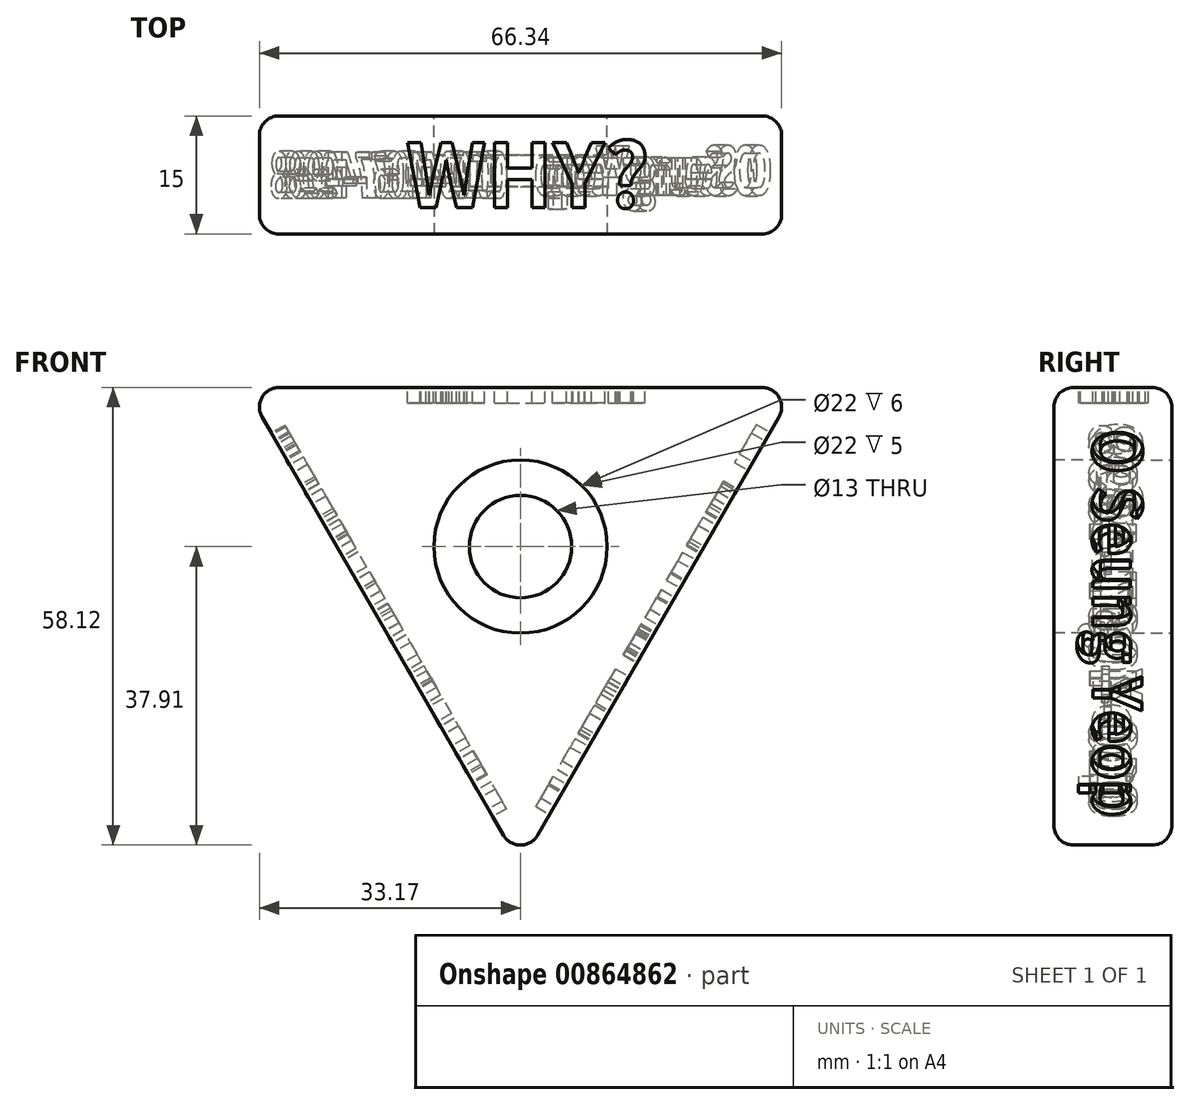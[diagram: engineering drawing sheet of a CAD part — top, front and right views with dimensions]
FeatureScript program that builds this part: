
annotation { "Feature Type Name" : "Feature", "Feature Type Description" : "" }
export const myFeature = defineFeature(function(context is Context, id is Id, definition is map)
    precondition{}
    {
        {
            var Q0;
            Q0=qCreatedBy(makeId("Front.planeOp"),FACE);
            var sketch = newSketch(context, id + "F0", { "sketchPlane" : qUnion([Q0])});
            skCircle(sketch, "E0.cCircle", {"center": v(0, 0) * mm, "radius": 20.2 * mm, "construction": true});
            skLineSegment(sketch, "E0.0", {"start": v(-35, 20.2) * mm, "end": v(35, 20.2) * mm});
            skLineSegment(sketch, "E0.1", {"start": v(35, 20.2) * mm, "end": v(0, -40.41) * mm});
            skLineSegment(sketch, "E0.2", {"start": v(0, -40.41) * mm, "end": v(-35, 20.2) * mm});
            skPoint(sketch, "E0.0.midPoint", {"position": v(0, 20.2) * mm});
            skSolve(sketch);
        }
        {
            var Q0;
            Q0 = qSketchRegion(id + "F0", true);
            extrude(context, id + "F1", {"entities" : qUnion([Q0]), "depth" : 15 * mm, "offsetDistance" : 25 * mm});
        }
        {
            var Q0;
            Q0=makeQuery(id+"F1.opExtrude","SWEPT_FACE",FACE,{"disambiguationData":[OSD([sQuery(id+"F0.wireOp",EDGE,"E0.0")])]});
            var sketch = newSketch(context, id + "F2", { "sketchPlane" : qUnion([Q0])});
            skText(sketch, "E1", { "text": "WHY?", "fontName": "NotoSansCJKkr-Bold.otf"});
            const initialGuessF2  = {"E1": [-0.01455, -0.01164, 1, 0, 0.00805]};
            skSetInitialGuess(sketch, initialGuessF2);
            skSolve(sketch);
        }
        {
            var Q0;
            Q0 = qSketchRegion(id + "F2", true);
            extrude(context, id + "F3", {"entities" : qUnion([Q0]), "operationType" : NewBodyOperationType.REMOVE, "oppositeDirection" : true, "depth" : 2 * mm, "offsetDistance" : 25 * mm});
        }
        {
            var Q0;
            Q0=makeQuery(id+"F1.opExtrude","CAP_FACE",FACE,{"disambiguationData":[OSD([sQuery(id+"F0.wireOp",EDGE,"E0.0"),sQuery(id+"F0.wireOp",EDGE,"E0.1"),sQuery(id+"F0.wireOp",EDGE,"E0.2")])],"isStart":false});
            var sketch = newSketch(context, id + "F4", { "sketchPlane" : qUnion([Q0])});
            skCircle(sketch, "E2", {"center": v(0, 0) * mm, "radius": 11 * mm});
            skSolve(sketch);
        }
        {
            var Q0;
            Q0=makeQuery(id+"F4.imprint","IMPRINT",FACE,{"disambiguationData":[TD([[makeQuery(id+"F4.imprint","IMPRINT",EDGE,{"derivedFrom":sQuery(id+"F4.wireOp",EDGE,"E2")}),1.0]])]});
            var Q1;
            Q1 = qSketchRegion(id + "F6", true);
            extrude(context, id + "F5", {"entities" : qUnion([Q0, Q1]), "operationType" : NewBodyOperationType.REMOVE, "oppositeDirection" : true, "depth" : 6 * mm, "offsetDistance" : 25 * mm});
        }
        {
            var Q0;
            Q0=makeQuery(id+"F1.opExtrude","CAP_FACE",FACE,{"disambiguationData":[OSD([sQuery(id+"F0.wireOp",EDGE,"E0.0"),sQuery(id+"F0.wireOp",EDGE,"E0.1"),sQuery(id+"F0.wireOp",EDGE,"E0.2")])],"isStart":true});
            var sketch = newSketch(context, id + "F6", { "sketchPlane" : qUnion([Q0])});
            skCircle(sketch, "E3", {"center": v(0, 0) * mm, "radius": 11 * mm});
            skSolve(sketch);
        }
        {
            var Q0;
            Q0=makeQuery(id+"F6.imprint","IMPRINT",FACE,{"disambiguationData":[TD([[makeQuery(id+"F6.imprint","IMPRINT",EDGE,{"derivedFrom":sQuery(id+"F6.wireOp",EDGE,"E3")}),1.0]])]});
            extrude(context, id + "F7", {"entities" : qUnion([Q0]), "operationType" : NewBodyOperationType.REMOVE, "oppositeDirection" : true, "depth" : 5 * mm, "offsetDistance" : 25 * mm});
        }
        {
            var Q0;
            Q0=makeQuery(id+"F5.boolean.opBoolean","COPY",FACE,{"derivedFrom":makeQuery(id+"F5.opExtrude","CAP_FACE",FACE,{"disambiguationData":[OSD([sQuery(id+"F4.wireOp",EDGE,"E2")])],"isStart":false})});
            var sketch = newSketch(context, id + "F8", { "sketchPlane" : qUnion([Q0])});
            skCircle(sketch, "E4", {"center": v(0, 0) * mm, "radius": 6.5 * mm});
            skSolve(sketch);
        }
        {
            var Q0;
            Q0=makeQuery(id+"F8.imprint","IMPRINT",FACE,{"disambiguationData":[TD([[makeQuery(id+"F8.imprint","IMPRINT",EDGE,{"derivedFrom":sQuery(id+"F8.wireOp",EDGE,"E4")}),1.0]])]});
            extrude(context, id + "F9", {"entities" : qUnion([Q0]), "operationType" : NewBodyOperationType.REMOVE, "oppositeDirection" : true, "depth" : 25 * mm, "offsetDistance" : 25 * mm});
        }
        {
            var Q0;
            Q0=makeQuery(id+"F1.opExtrude","SWEPT_FACE",FACE,{"disambiguationData":[OSD([sQuery(id+"F0.wireOp",EDGE,"E0.1")])]});
            var sketch = newSketch(context, id + "F10", { "sketchPlane" : qUnion([Q0])});
            skText(sketch, "E5", { "text": "O Seung Yeop", "fontName": "NotoSansCJKkr-Bold.otf"});
            const initialGuessF10  = {"E5": [-0.01004, 0.02888, 0, -1, 0.00608]};
            skSetInitialGuess(sketch, initialGuessF10);
            skSolve(sketch);
        }
        {
            var Q0;
            Q0 = qSketchRegion(id + "F10", true);
            extrude(context, id + "F11", {"entities" : qUnion([Q0]), "operationType" : NewBodyOperationType.REMOVE, "oppositeDirection" : true, "depth" : 2 * mm, "offsetDistance" : 25 * mm});
        }
        {
            var Q0;
            Q0=makeQuery(id+"F1.opExtrude","SWEPT_FACE",FACE,{"disambiguationData":[OSD([sQuery(id+"F0.wireOp",EDGE,"E0.2")])]});
            var sketch = newSketch(context, id + "F12", { "sketchPlane" : qUnion([Q0])});
            skText(sketch, "E6", { "text": "010-4067-4998", "fontName": "NotoSansCJKkr-Bold.otf"});
            const initialGuessF12  = {"E6": [0.01042, -0.02829, 0, 1, 0.00568]};
            skSetInitialGuess(sketch, initialGuessF12);
            skSolve(sketch);
        }
        {
            var Q0;
            Q0 = qSketchRegion(id + "F12", true);
            extrude(context, id + "F13", {"entities" : qUnion([Q0]), "operationType" : NewBodyOperationType.REMOVE, "oppositeDirection" : true, "depth" : 2 * mm, "offsetDistance" : 25 * mm});
        }
        {
            var Q0;
            Q0=makeQuery(id+"F1.opExtrude","CAP_EDGE",EDGE,{"disambiguationData":[OSD([sQuery(id+"F0.wireOp",EDGE,"E0.0")])],"isStart":true});
            var Q1;
            Q1=makeQuery(id+"F1.opExtrude","CAP_EDGE",EDGE,{"disambiguationData":[OSD([sQuery(id+"F0.wireOp",EDGE,"E0.2")])],"isStart":true});
            var Q2;
            Q2=makeQuery(id+"F1.opExtrude","CAP_EDGE",EDGE,{"disambiguationData":[OSD([sQuery(id+"F0.wireOp",EDGE,"E0.1")])],"isStart":true});
            var Q3;
            Q3=makeQuery(id+"F1.opExtrude","CAP_EDGE",EDGE,{"disambiguationData":[OSD([sQuery(id+"F0.wireOp",EDGE,"E0.2")])],"isStart":false});
            var Q4;
            Q4=makeQuery(id+"F1.opExtrude","CAP_EDGE",EDGE,{"disambiguationData":[OSD([sQuery(id+"F0.wireOp",EDGE,"E0.0")])],"isStart":false});
            var Q5;
            Q5=makeQuery(id+"F1.opExtrude","SWEPT_EDGE",EDGE,{"disambiguationData":[OSD([sQuery(id+"F0.wireOp",EDGE,"E0.0"),sQuery(id+"F0.wireOp",EDGE,"E0.2")])]});
            var Q6;
            Q6=makeQuery(id+"F1.opExtrude","SWEPT_EDGE",EDGE,{"disambiguationData":[OSD([sQuery(id+"F0.wireOp",EDGE,"E0.0"),sQuery(id+"F0.wireOp",EDGE,"E0.1")])]});
            var Q7;
            Q7=makeQuery(id+"F1.opExtrude","CAP_EDGE",EDGE,{"disambiguationData":[OSD([sQuery(id+"F0.wireOp",EDGE,"E0.1")])],"isStart":false});
            var Q8;
            Q8=makeQuery(id+"F1.opExtrude","SWEPT_EDGE",EDGE,{"disambiguationData":[OSD([sQuery(id+"F0.wireOp",EDGE,"E0.1"),sQuery(id+"F0.wireOp",EDGE,"E0.2")])]});
            fillet(context, id + "F14", {"entities" : qUnion([Q0, Q1, Q2, Q3, Q4, Q5, Q6, Q7, Q8]), "radius" : 2.5 * mm, "tangentPropagation" : true, "allowEdgeOverflow" : false});
        }
    });
